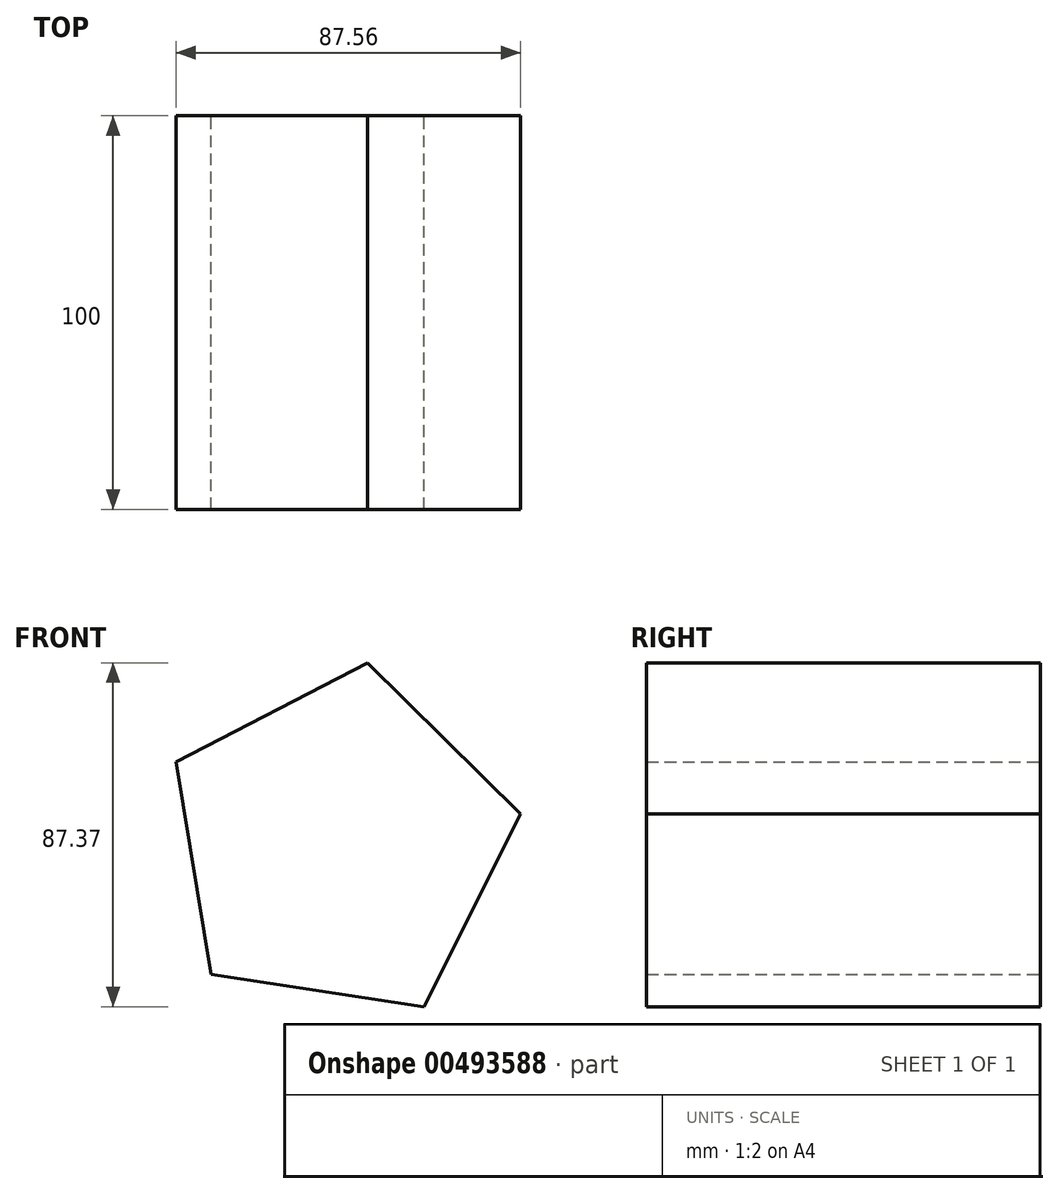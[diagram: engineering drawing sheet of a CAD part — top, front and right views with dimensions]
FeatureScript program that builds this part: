
annotation { "Feature Type Name" : "Feature", "Feature Type Description" : "" }
export const myFeature = defineFeature(function(context is Context, id is Id, definition is map)
    precondition{}
    {
        {
            var Q0;
            Q0=qCreatedBy(makeId("Front.planeOp"),FACE);
            var sketch = newSketch(context, id + "F0", { "sketchPlane" : qUnion([Q0])});
            skCircle(sketch, "E0.cCircle", {"center": v(0, 0) * mm, "radius": 46.56 * mm, "construction": true});
            skLineSegment(sketch, "E0.0", {"start": v(-32.7, -33.14) * mm, "end": v(-41.62, 20.86) * mm});
            skLineSegment(sketch, "E0.1", {"start": v(-41.62, 20.86) * mm, "end": v(6.98, 46.03) * mm});
            skLineSegment(sketch, "E0.2", {"start": v(6.98, 46.03) * mm, "end": v(45.94, 7.58) * mm});
            skLineSegment(sketch, "E0.3", {"start": v(45.94, 7.58) * mm, "end": v(21.4, -41.34) * mm});
            skLineSegment(sketch, "E0.4", {"start": v(21.4, -41.34) * mm, "end": v(-32.7, -33.14) * mm});
            skSolve(sketch);
        }
        {
            var Q0;
            Q0=makeQuery(id+"F0.imprint","IMPRINT",FACE,{"disambiguationData":[TD([[makeQuery(id+"F0.imprint","IMPRINT",EDGE,{"derivedFrom":sQuery(id+"F0.wireOp",EDGE,"E0.0")}),-1.0]])]});
            extrude(context, id + "F1", {"entities" : qUnion([Q0]), "endBound" : BoundingType.SYMMETRIC, "depth" : 100 * mm});
        }
    });
